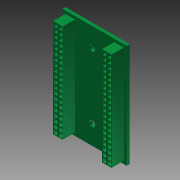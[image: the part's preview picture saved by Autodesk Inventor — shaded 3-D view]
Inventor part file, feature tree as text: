
AUTODESK INVENTOR PART (.ipt)
format: ipt  version: 2012 (Build 160160000, 160)  size: 446,464 bytes
history: native  units: in
note: dims shown in document units (in); Inventor stores cm internally (conversion verified against a paired STEP export)
features: extrude x2, sketch x1
ambient origin geometry x8: Origin, YZ Plane, XZ Plane, XY Plane, X Axis, Y Axis, Z Axis, Center Point
bodies: Solid1 (feature_tree)
feature tree (3):
  sketch  "Sketch1"  dims[d3=2.0069in d4=0.1969in d5=0.0591in d6=0.0591in d7=0.0669in d8=0.0669in d9=0.1in d10=0.0669in d11=0.0669in d12=0.0197in d13=0.0197in d14=0.0197in d15=0.0669in d16=0.0669in d17=0.1in d18=0.0669in d19=0.0669in d21=0.1in d22=0.1in d23=0.0197in d24=3.937in d26=0.2in d27=0.3937in d29=1.0in d31=0.7874in d33=1.0in d34=0.3937in d36=1.0in d38=0.0591in d39=0.0591in d40=0.6075in d41=0.6075in d42=0.3937in d43=0.3937in d44=0.1181in d45=0.1181in d46=0.063in d47=0.0in d48=0.315in d49=0.0in]
  extrude  "Extrusion1"  Depth=0.1969in
  extrude  "Extrusion2"  Depth=0.0591in
